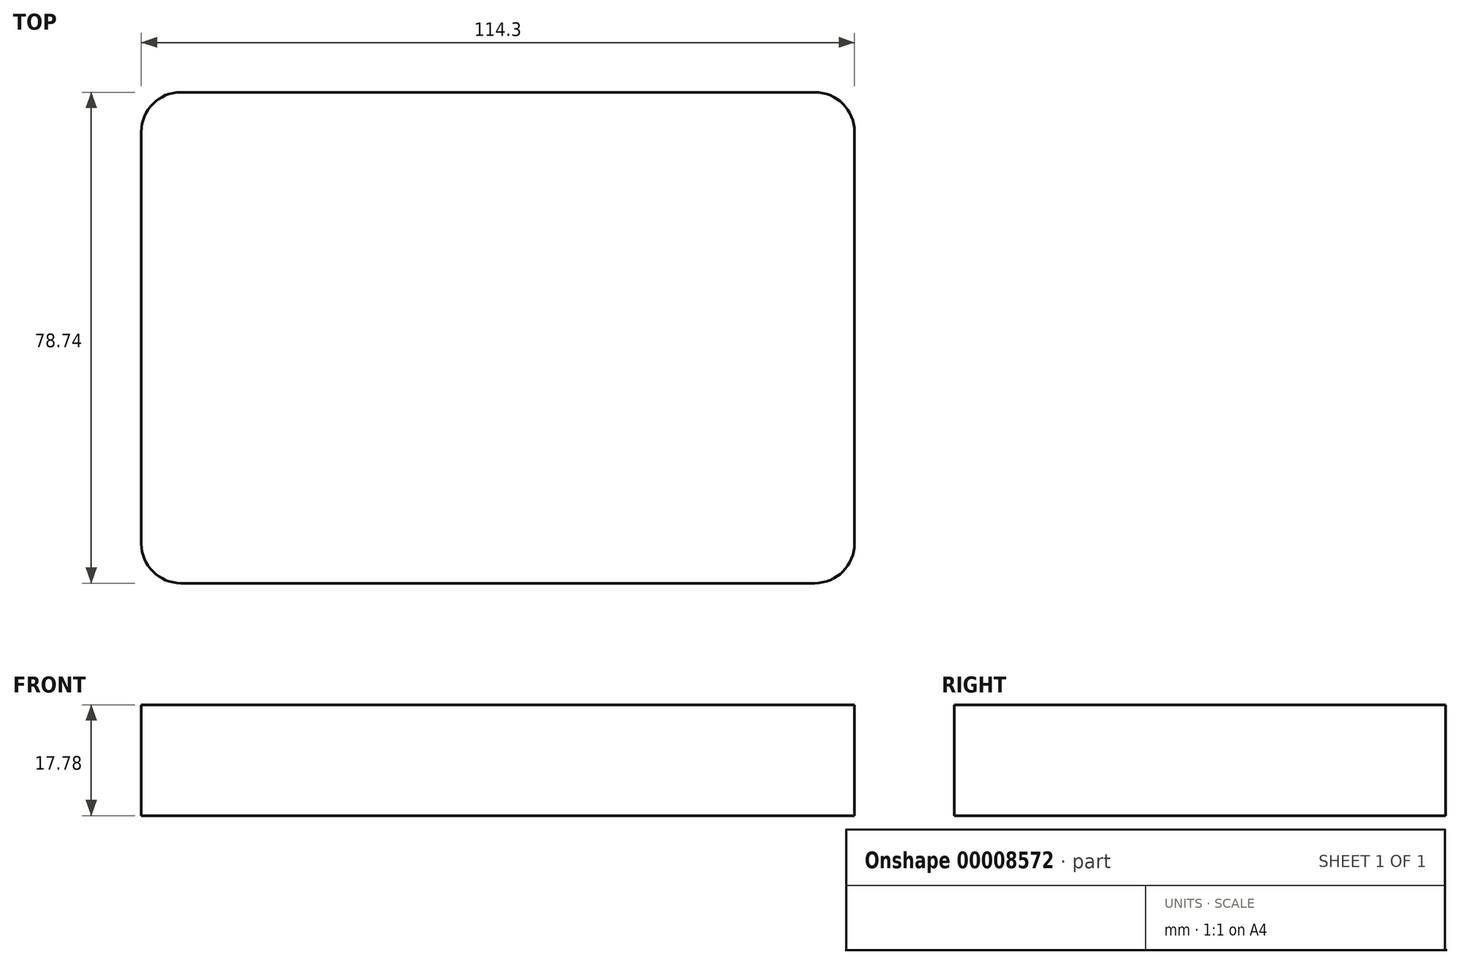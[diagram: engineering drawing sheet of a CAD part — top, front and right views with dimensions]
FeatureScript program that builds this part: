
annotation { "Feature Type Name" : "Feature", "Feature Type Description" : "" }
export const myFeature = defineFeature(function(context is Context, id is Id, definition is map)
    precondition{}
    {
        {
            var Q0;
            Q0=qCreatedBy(makeId("Top.planeOp"),FACE);
            var sketch = newSketch(context, id + "F0", { "sketchPlane" : qUnion([Q0])});
            skLineSegment(sketch, "E0.bottom", {"start": v(-50.8, 39.37) * mm, "end": v(50.8, 39.37) * mm});
            skLineSegment(sketch, "E0.top", {"start": v(-50.8, -39.37) * mm, "end": v(50.8, -39.37) * mm});
            skLineSegment(sketch, "E0.left", {"start": v(-57.15, 33.02) * mm, "end": v(-57.15, -33.02) * mm});
            skLineSegment(sketch, "E0.right", {"start": v(57.15, 33.02) * mm, "end": v(57.15, -33.02) * mm});
            skLineSegment(sketch, "E1", {"start": v(0, 39.37) * mm, "end": v(0, -39.37) * mm, "construction": true});
            skLineSegment(sketch, "E2", {"start": v(57.15, 0) * mm, "end": v(-57.15, 0) * mm, "construction": true});
            skPoint(sketch, "E3.visualSharp", {"position": v(-57.15, -39.37) * mm});
            skArc(sketch, "E3.filletArc", {"start": v(-57.15, -33.02) * mm, "mid": v(-55.3, -37.51) * mm, "end": v(-50.8, -39.37) * mm});
            skPoint(sketch, "E4.visualSharp", {"position": v(-57.15, 39.37) * mm});
            skArc(sketch, "E4.filletArc", {"start": v(-50.8, 39.37) * mm, "mid": v(-55.3, 37.51) * mm, "end": v(-57.15, 33.02) * mm});
            skPoint(sketch, "E5.visualSharp", {"position": v(57.15, 39.37) * mm});
            skArc(sketch, "E5.filletArc", {"start": v(57.15, 33.02) * mm, "mid": v(55.3, 37.51) * mm, "end": v(50.8, 39.37) * mm});
            skPoint(sketch, "E6.visualSharp", {"position": v(57.15, -39.37) * mm});
            skArc(sketch, "E6.filletArc", {"start": v(50.8, -39.37) * mm, "mid": v(55.3, -37.51) * mm, "end": v(57.15, -33.02) * mm});
            skSolve(sketch);
        }
        {
            var Q0;
            Q0 = qSketchRegion(id + "F0", true);
            extrude(context, id + "F1", {"entities" : qUnion([Q0]), "depth" : 17.78 * mm});
        }
    });
